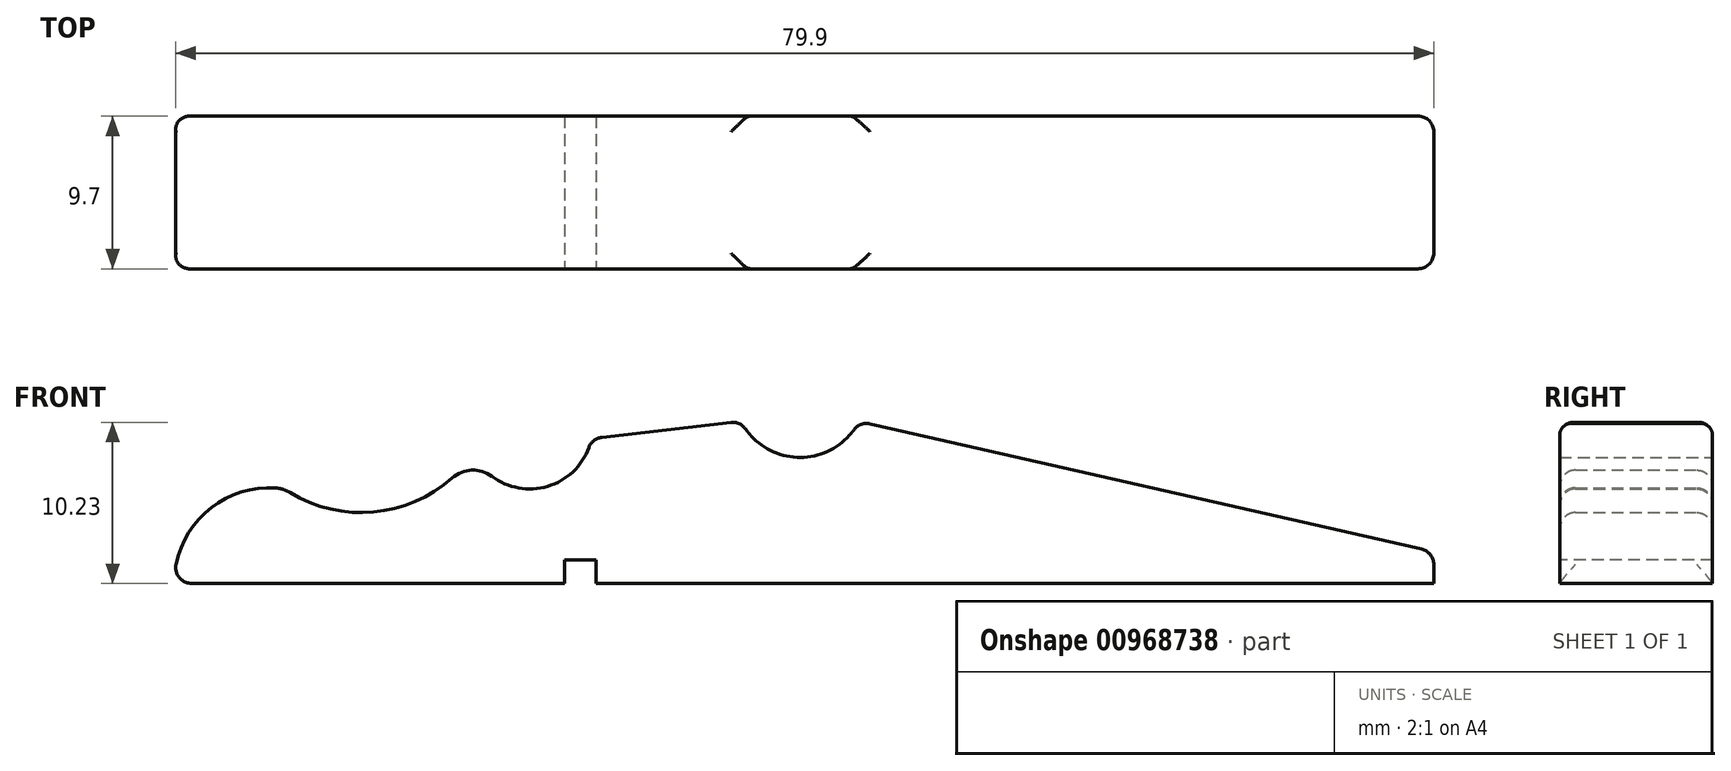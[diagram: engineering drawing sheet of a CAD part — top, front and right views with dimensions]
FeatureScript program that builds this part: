
annotation { "Feature Type Name" : "Feature", "Feature Type Description" : "" }
export const myFeature = defineFeature(function(context is Context, id is Id, definition is map)
    precondition{}
    {
        {
            var Q0;
            Q0=qCreatedBy(makeId("Front.planeOp"),FACE);
            var sketch = newSketch(context, id + "F0", { "sketchPlane" : qUnion([Q0])});
            skLineSegment(sketch, "E0", {"start": v(0, 0) * mm, "end": v(80, 0) * mm});
            skLineSegment(sketch, "E1", {"start": v(19, 0) * mm, "end": v(19, 8.2) * mm, "construction": true});
            skLineSegment(sketch, "E2", {"start": v(26.5, 0) * mm, "end": v(26.5, 9.2) * mm, "construction": true});
            skLineSegment(sketch, "E3", {"start": v(36, 0) * mm, "end": v(36, 10.3) * mm, "construction": true});
            skLineSegment(sketch, "E4", {"start": v(7, 0) * mm, "end": v(7, 6) * mm, "construction": true});
            skLineSegment(sketch, "E5", {"start": v(43.5, 0) * mm, "end": v(43.5, 10.3) * mm, "construction": true});
            skArc(sketch, "E6", {"start": v(7, 6) * mm, "mid": v(2.12, 4.6) * mm, "end": v(0, 0) * mm});
            skArc(sketch, "E7", {"start": v(7, 6) * mm, "mid": v(13.45, 4.64) * mm, "end": v(19, 8.2) * mm});
            skLineSegment(sketch, "E8", {"start": v(11.88, 13.2) * mm, "end": v(11.88, 4.5) * mm, "construction": true});
            skArc(sketch, "E9", {"start": v(19, 8.2) * mm, "mid": v(23.1, 6.04) * mm, "end": v(26.5, 9.2) * mm});
            skLineSegment(sketch, "E10", {"start": v(22.58, 10) * mm, "end": v(22.58, 6) * mm, "construction": true});
            skLineSegment(sketch, "E11", {"start": v(26.5, 9.2) * mm, "end": v(36, 10.3) * mm});
            skArc(sketch, "E12", {"start": v(36, 10.3) * mm, "mid": v(39.75, 8) * mm, "end": v(43.5, 10.3) * mm});
            skPoint(sketch, "E13", {"position": v(39.75, 8) * mm});
            skLineSegment(sketch, "E14", {"start": v(80, 0) * mm, "end": v(80, 2) * mm});
            skLineSegment(sketch, "E15", {"start": v(43.5, 10.3) * mm, "end": v(80, 2) * mm});
            skSolve(sketch);
        }
        {
            var Q0;
            Q0 = qSketchRegion(id + "F0", true);
            extrude(context, id + "F1", {"entities" : qUnion([Q0]), "depth" : 9.7 * mm, "offsetDistance" : 25 * mm});
        }
        {
            var Q0;
            Q0=makeQuery(id+"F1.opExtrude","CAP_FACE",FACE,{"disambiguationData":[OSD([sQuery(id+"F0.wireOp",EDGE,"E0"),sQuery(id+"F0.wireOp",EDGE,"E6"),sQuery(id+"F0.wireOp",EDGE,"E7"),sQuery(id+"F0.wireOp",EDGE,"E9"),sQuery(id+"F0.wireOp",EDGE,"E11"),sQuery(id+"F0.wireOp",EDGE,"E12"),sQuery(id+"F0.wireOp",EDGE,"E14"),sQuery(id+"F0.wireOp",EDGE,"E15")])],"isStart":false});
            var sketch = newSketch(context, id + "F2", { "sketchPlane" : qUnion([Q0])});
            skLineSegment(sketch, "E16.bottom", {"start": v(24.8, 0) * mm, "end": v(26.8, 0) * mm});
            skLineSegment(sketch, "E16.top", {"start": v(24.8, 1.5) * mm, "end": v(26.8, 1.5) * mm});
            skLineSegment(sketch, "E16.left", {"start": v(24.8, 0) * mm, "end": v(24.8, 1.5) * mm});
            skLineSegment(sketch, "E16.right", {"start": v(26.8, 0) * mm, "end": v(26.8, 1.5) * mm});
            skSolve(sketch);
        }
        {
            var Q0;
            Q0=makeQuery(id+"F1.opExtrude","SWEPT_EDGE",EDGE,{"disambiguationData":[OSD([sQuery(id+"F0.wireOp",EDGE,"E7"),sQuery(id+"F0.wireOp",EDGE,"E9")])]});
            var Q1;
            Q1=makeQuery(id+"F1.opExtrude","SWEPT_EDGE",EDGE,{"disambiguationData":[OSD([sQuery(id+"F0.wireOp",EDGE,"E6"),sQuery(id+"F0.wireOp",EDGE,"E7")])]});
            fillet(context, id + "F3", {"entities" : qUnion([Q0, Q1]), "radius" : 2 * mm, "tangentPropagation" : true, "allowEdgeOverflow" : false});
        }
        {
            var Q0;
            Q0=makeQuery(id+"F1.opExtrude","SWEPT_EDGE",EDGE,{"disambiguationData":[OSD([sQuery(id+"F0.wireOp",EDGE,"E9"),sQuery(id+"F0.wireOp",EDGE,"E11")])]});
            var Q1;
            Q1=makeQuery(id+"F1.opExtrude","SWEPT_EDGE",EDGE,{"disambiguationData":[OSD([sQuery(id+"F0.wireOp",EDGE,"E11"),sQuery(id+"F0.wireOp",EDGE,"E12")])]});
            var Q2;
            Q2=makeQuery(id+"F1.opExtrude","SWEPT_EDGE",EDGE,{"disambiguationData":[OSD([sQuery(id+"F0.wireOp",EDGE,"E12"),sQuery(id+"F0.wireOp",EDGE,"E15")])]});
            var Q3;
            Q3=makeQuery(id+"F1.opExtrude","SWEPT_EDGE",EDGE,{"disambiguationData":[OSD([sQuery(id+"F0.wireOp",EDGE,"E14"),sQuery(id+"F0.wireOp",EDGE,"E15")])]});
            var Q4;
            Q4=makeQuery(id+"F1.opExtrude","SWEPT_FACE",FACE,{"disambiguationData":[OSD([sQuery(id+"F0.wireOp",EDGE,"E15")])]});
            var Q5;
            Q5=makeQuery(id+"F1.opExtrude","SWEPT_FACE",FACE,{"disambiguationData":[OSD([sQuery(id+"F0.wireOp",EDGE,"E11")])]});
            var Q6;
            Q6=makeQuery(id+"F1.opExtrude","SWEPT_FACE",FACE,{"disambiguationData":[OSD([sQuery(id+"F0.wireOp",EDGE,"E6")])]});
            var Q7;
            Q7=makeQuery(id+"F1.opExtrude","CAP_EDGE",EDGE,{"disambiguationData":[OSD([sQuery(id+"F0.wireOp",EDGE,"E14")])],"isStart":false});
            var Q8;
            Q8=makeQuery(id+"F1.opExtrude","CAP_EDGE",EDGE,{"disambiguationData":[OSD([sQuery(id+"F0.wireOp",EDGE,"E14")])],"isStart":true});
            fillet(context, id + "F4", {"entities" : qUnion([Q0, Q1, Q2, Q3, Q4, Q5, Q6, Q7, Q8]), "radius" : 1 * mm, "tangentPropagation" : true, "allowEdgeOverflow" : false});
        }
        {
            var Q0;
            Q0 = qSketchRegion(id + "F2", true);
            extrude(context, id + "F5", {"entities" : qUnion([Q0]), "operationType" : NewBodyOperationType.REMOVE, "endBound" : BoundingType.THROUGH_ALL, "oppositeDirection" : true, "depth" : 25 * mm, "offsetDistance" : 25 * mm});
        }
    });
